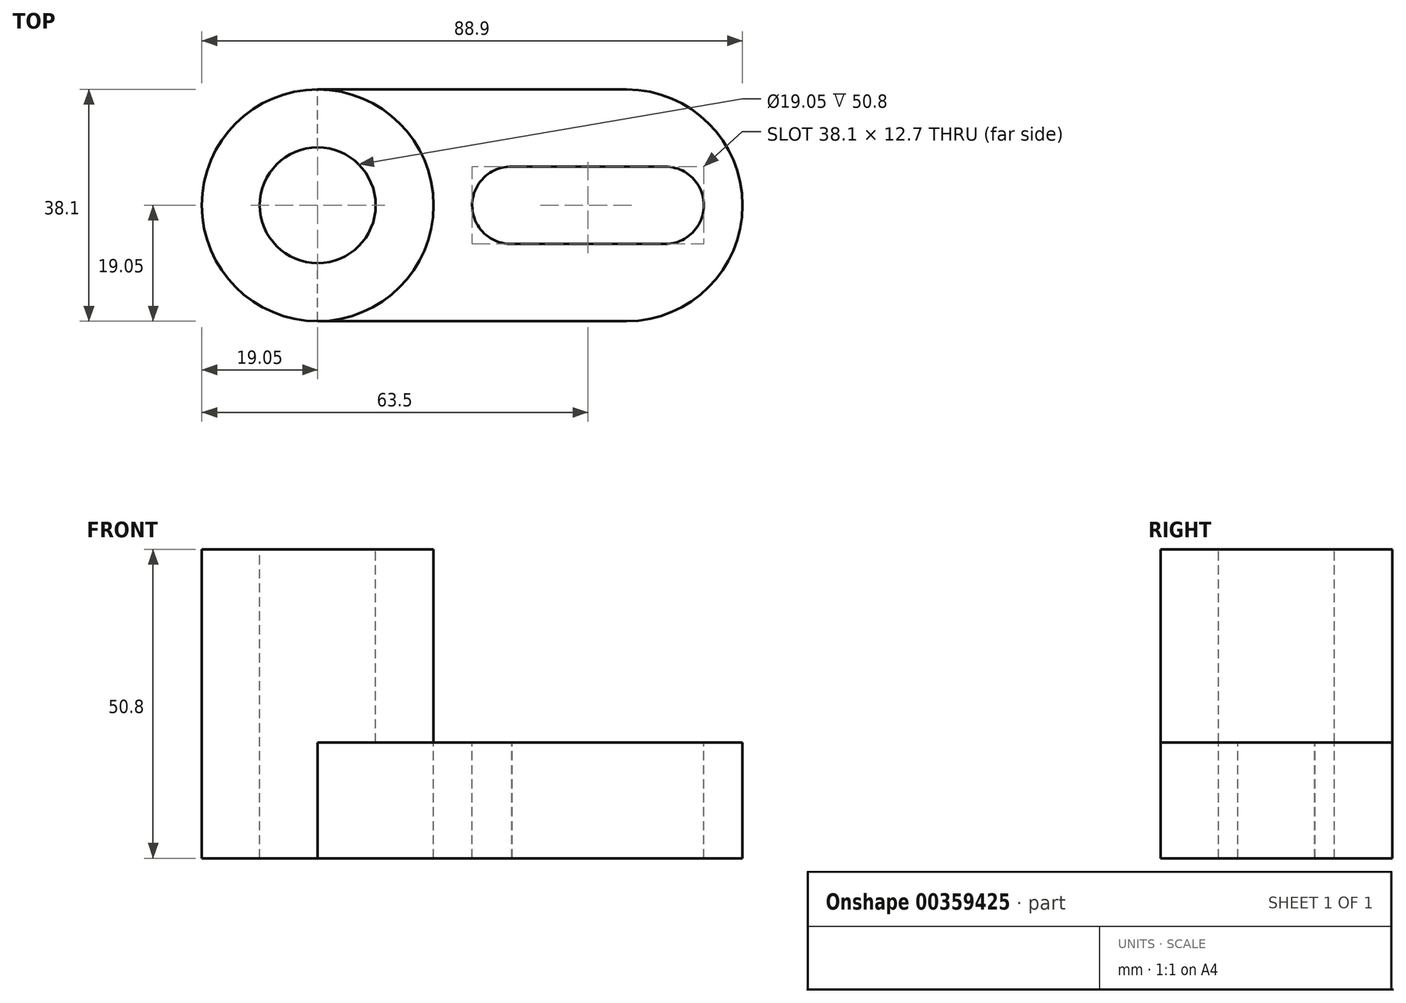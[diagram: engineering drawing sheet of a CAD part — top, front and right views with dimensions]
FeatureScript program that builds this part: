
annotation { "Feature Type Name" : "Feature", "Feature Type Description" : "" }
export const myFeature = defineFeature(function(context is Context, id is Id, definition is map)
    precondition{}
    {
        {
            var Q0;
            Q0=qCreatedBy(makeId("Front.planeOp"),FACE);
            var sketch = newSketch(context, id + "F0", { "sketchPlane" : qUnion([Q0])});
            skLineSegment(sketch, "E0", {"start": v(0, 0) * mm, "end": v(0, 50.8) * mm});
            skLineSegment(sketch, "E1", {"start": v(0, 50.8) * mm, "end": v(38.1, 50.8) * mm});
            skLineSegment(sketch, "E2", {"start": v(38.1, 50.8) * mm, "end": v(38.1, 19.05) * mm});
            skLineSegment(sketch, "E3", {"start": v(38.1, 19.05) * mm, "end": v(88.9, 19.05) * mm});
            skLineSegment(sketch, "E4", {"start": v(88.9, 19.05) * mm, "end": v(88.9, 0) * mm});
            skLineSegment(sketch, "E5", {"start": v(88.9, 0) * mm, "end": v(0, 0) * mm});
            skSolve(sketch);
        }
        {
            var Q0;
            Q0 = qSketchRegion(id + "F0", true);
            extrude(context, id + "F1", {"entities" : qUnion([Q0]), "depth" : 38.1 * mm});
        }
        {
            var Q0;
            Q0=makeQuery(id+"F1.opExtrude","SWEPT_FACE",FACE,{"disambiguationData":[OSD([sQuery(id+"F0.wireOp",EDGE,"E1")])]});
            var sketch = newSketch(context, id + "F2", { "sketchPlane" : qUnion([Q0])});
            skLineSegment(sketch, "E6", {"start": v(19.05, 0) * mm, "end": v(19.05, 0) * mm});
            skLineSegment(sketch, "E7", {"start": v(38.1, -19.05) * mm, "end": v(38.1, -19.05) * mm});
            skLineSegment(sketch, "E8", {"start": v(19.05, -38.1) * mm, "end": v(19.05, -38.1) * mm});
            skLineSegment(sketch, "E9", {"start": v(0, -19.05) * mm, "end": v(0, -19.05) * mm});
            skPoint(sketch, "E10.visualSharp", {"position": v(0, 0) * mm});
            skArc(sketch, "E10.filletArc", {"start": v(19.05, 0) * mm, "mid": v(5.58, -5.58) * mm, "end": v(0, -19.05) * mm});
            skPoint(sketch, "E11.visualSharp", {"position": v(38.1, 0) * mm});
            skArc(sketch, "E11.filletArc", {"start": v(38.1, -19.05) * mm, "mid": v(32.52, -5.58) * mm, "end": v(19.05, 0) * mm});
            skPoint(sketch, "E12.visualSharp", {"position": v(38.1, -38.1) * mm});
            skArc(sketch, "E12.filletArc", {"start": v(19.05, -38.1) * mm, "mid": v(32.52, -32.52) * mm, "end": v(38.1, -19.05) * mm});
            skPoint(sketch, "E13.visualSharp", {"position": v(0, -38.1) * mm});
            skArc(sketch, "E13.filletArc", {"start": v(0, -19.05) * mm, "mid": v(5.58, -32.52) * mm, "end": v(19.05, -38.1) * mm});
            skSolve(sketch);
        }
        {
            var Q0;
            {var subQ0=sQuery(id+"F2.wireOp",EDGE,"E13.filletArc");Q0=makeQuery(id+"F2.imprint","IMPRINT",FACE,{"disambiguationData":[TD([[makeQuery(id+"F2.imprint","IMPRINT",EDGE,{"derivedFrom":subQ0}),-1.0]])]});}
            var Q1;
            {var subQ0=sQuery(id+"F2.wireOp",EDGE,"E10.filletArc");Q1=makeQuery(id+"F2.imprint","IMPRINT",FACE,{"disambiguationData":[TD([[makeQuery(id+"F2.imprint","IMPRINT",EDGE,{"derivedFrom":subQ0}),-1.0]])]});}
            extrude(context, id + "F3", {"entities" : qUnion([Q0, Q1]), "operationType" : NewBodyOperationType.REMOVE, "oppositeDirection" : true, "depth" : 50.8 * mm});
        }
        {
            var Q0;
            Q0=makeQuery(id+"F1.opExtrude","SWEPT_FACE",FACE,{"disambiguationData":[OSD([sQuery(id+"F0.wireOp",EDGE,"E1")])]});
            var sketch = newSketch(context, id + "F4", { "sketchPlane" : qUnion([Q0])});
            skLineSegment(sketch, "E14", {"start": v(19.05, 0) * mm, "end": v(0, 0) * mm});
            skLineSegment(sketch, "E15", {"start": v(0, 0) * mm, "end": v(0, -38.1) * mm});
            skLineSegment(sketch, "E16", {"start": v(0, -38.1) * mm, "end": v(19.05, -38.1) * mm});
            skLineSegment(sketch, "E17", {"start": v(38.1, -19.05) * mm, "end": v(38.1, -19.05) * mm});
            skPoint(sketch, "E18.visualSharp", {"position": v(38.1, 0) * mm});
            skArc(sketch, "E18.filletArc", {"start": v(38.1, -19.05) * mm, "mid": v(32.52, -5.58) * mm, "end": v(19.05, 0) * mm});
            skPoint(sketch, "E19.visualSharp", {"position": v(38.1, -38.1) * mm});
            skArc(sketch, "E19.filletArc", {"start": v(19.05, -38.1) * mm, "mid": v(32.52, -32.52) * mm, "end": v(38.1, -19.05) * mm});
            skSolve(sketch);
        }
        {
            var Q0;
            {var subQ0=sQuery(id+"F4.wireOp",EDGE,"E19.filletArc");Q0=makeQuery(id+"F4.imprint","IMPRINT",FACE,{"disambiguationData":[TD([[makeQuery(id+"F4.imprint","IMPRINT",EDGE,{"derivedFrom":subQ0}),-1.0]])]});}
            var Q1;
            {var subQ0=sQuery(id+"F4.wireOp",EDGE,"E18.filletArc");Q1=makeQuery(id+"F4.imprint","IMPRINT",FACE,{"disambiguationData":[TD([[makeQuery(id+"F4.imprint","IMPRINT",EDGE,{"derivedFrom":subQ0}),-1.0]])]});}
            extrude(context, id + "F5", {"entities" : qUnion([Q0, Q1]), "operationType" : NewBodyOperationType.REMOVE, "oppositeDirection" : true, "depth" : 31.75 * mm});
        }
        {
            var Q0;
            {var subQ0=sQuery(id+"F0.wireOp",EDGE,"E2");var subQ1=sQuery(id+"F0.wireOp",EDGE,"E1");Q0=makeQuery(id+"F5.boolean.opBoolean","MERGE",FACE,{"derivedFrom":[makeQuery(id+"F1.opExtrude","SWEPT_FACE",FACE,{"disambiguationData":[OSD([sQuery(id+"F0.wireOp",EDGE,"E3")])]}),makeQuery(id+"F5.opExtrude","CAP_FACE",FACE,{"disambiguationData":[OSD([subQ1,subQ0,sQuery(id+"F4.wireOp",EDGE,"E18.filletArc")])],"isStart":false}),makeQuery(id+"F5.opExtrude","CAP_FACE",FACE,{"disambiguationData":[OSD([subQ1,subQ0,sQuery(id+"F4.wireOp",EDGE,"E19.filletArc")])],"isStart":false})]});}
            var sketch = newSketch(context, id + "F6", { "sketchPlane" : qUnion([Q0])});
            skLineSegment(sketch, "E20", {"start": v(19.05, 0) * mm, "end": v(19.05, -38.1) * mm});
            skLineSegment(sketch, "E21", {"start": v(19.05, -38.1) * mm, "end": v(69.85, -38.1) * mm});
            skLineSegment(sketch, "E22", {"start": v(88.9, -19.05) * mm, "end": v(88.9, -19.05) * mm});
            skLineSegment(sketch, "E23", {"start": v(69.85, 0) * mm, "end": v(19.05, 0) * mm});
            skPoint(sketch, "E24.visualSharp", {"position": v(88.9, 0) * mm});
            skArc(sketch, "E24.filletArc", {"start": v(88.9, -19.05) * mm, "mid": v(83.32, -5.58) * mm, "end": v(69.85, 0) * mm});
            skPoint(sketch, "E25.visualSharp", {"position": v(88.9, -38.1) * mm});
            skArc(sketch, "E25.filletArc", {"start": v(69.85, -38.1) * mm, "mid": v(83.32, -32.52) * mm, "end": v(88.9, -19.05) * mm});
            skSolve(sketch);
        }
        {
            var Q0;
            Q0=makeQuery(id+"F6.imprint","IMPRINT",FACE,{"disambiguationData":[TD([[makeQuery(id+"F6.imprint","IMPRINT",EDGE,{"derivedFrom":sQuery(id+"F6.wireOp",EDGE,"E20")}),1.0]])]});
            var Q1;
            {var subQ0=sQuery(id+"F6.wireOp",EDGE,"E24.filletArc");Q1=makeQuery(id+"F6.imprint","IMPRINT",FACE,{"disambiguationData":[TD([[makeQuery(id+"F6.imprint","IMPRINT",EDGE,{"derivedFrom":subQ0}),-1.0]])]});}
            var Q2;
            {var subQ0=sQuery(id+"F6.wireOp",EDGE,"E25.filletArc");Q2=makeQuery(id+"F6.imprint","IMPRINT",FACE,{"disambiguationData":[TD([[makeQuery(id+"F6.imprint","IMPRINT",EDGE,{"derivedFrom":subQ0}),-1.0]])]});}
            extrude(context, id + "F7", {"entities" : qUnion([Q0, Q1, Q2]), "operationType" : NewBodyOperationType.REMOVE, "oppositeDirection" : true, "depth" : 25.4 * mm});
        }
        {
            var Q0;
            Q0=makeQuery(id+"F1.opExtrude","SWEPT_FACE",FACE,{"disambiguationData":[OSD([sQuery(id+"F0.wireOp",EDGE,"E1")])]});
            var sketch = newSketch(context, id + "F8", { "sketchPlane" : qUnion([Q0])});
            skCircle(sketch, "E26", {"center": v(19.05, -19.05) * mm, "radius": 9.53 * mm});
            skSolve(sketch);
        }
        {
            var Q0;
            Q0 = qSketchRegion(id + "F8", true);
            extrude(context, id + "F9", {"entities" : qUnion([Q0]), "operationType" : NewBodyOperationType.REMOVE, "oppositeDirection" : true, "depth" : 63.5 * mm});
        }
        {
            var Q0;
            {var subQ0=sQuery(id+"F0.wireOp",EDGE,"E2");var subQ1=sQuery(id+"F0.wireOp",EDGE,"E1");Q0=makeQuery(id+"F5.boolean.opBoolean","MERGE",FACE,{"derivedFrom":[makeQuery(id+"F1.opExtrude","SWEPT_FACE",FACE,{"disambiguationData":[OSD([sQuery(id+"F0.wireOp",EDGE,"E3")])]}),makeQuery(id+"F5.opExtrude","CAP_FACE",FACE,{"disambiguationData":[OSD([subQ1,subQ0,sQuery(id+"F4.wireOp",EDGE,"E18.filletArc")])],"isStart":false}),makeQuery(id+"F5.opExtrude","CAP_FACE",FACE,{"disambiguationData":[OSD([subQ1,subQ0,sQuery(id+"F4.wireOp",EDGE,"E19.filletArc")])],"isStart":false})]});}
            var sketch = newSketch(context, id + "F10", { "sketchPlane" : qUnion([Q0])});
            skCircle(sketch, "E27", {"center": v(50.8, -19.05) * mm, "radius": 6.35 * mm});
            skCircle(sketch, "E28", {"center": v(76.2, -19.05) * mm, "radius": 6.35 * mm});
            skLineSegment(sketch, "E29", {"start": v(50.94, -12.7) * mm, "end": v(76.2, -12.7) * mm});
            skLineSegment(sketch, "E30", {"start": v(50.55, -25.4) * mm, "end": v(76.2, -25.4) * mm});
            skSolve(sketch);
        }
        {
            var Q0;
            Q0 = qSketchRegion(id + "F10", true);
            extrude(context, id + "F11", {"entities" : qUnion([Q0]), "operationType" : NewBodyOperationType.REMOVE, "oppositeDirection" : true, "depth" : 25.4 * mm});
        }
    });
